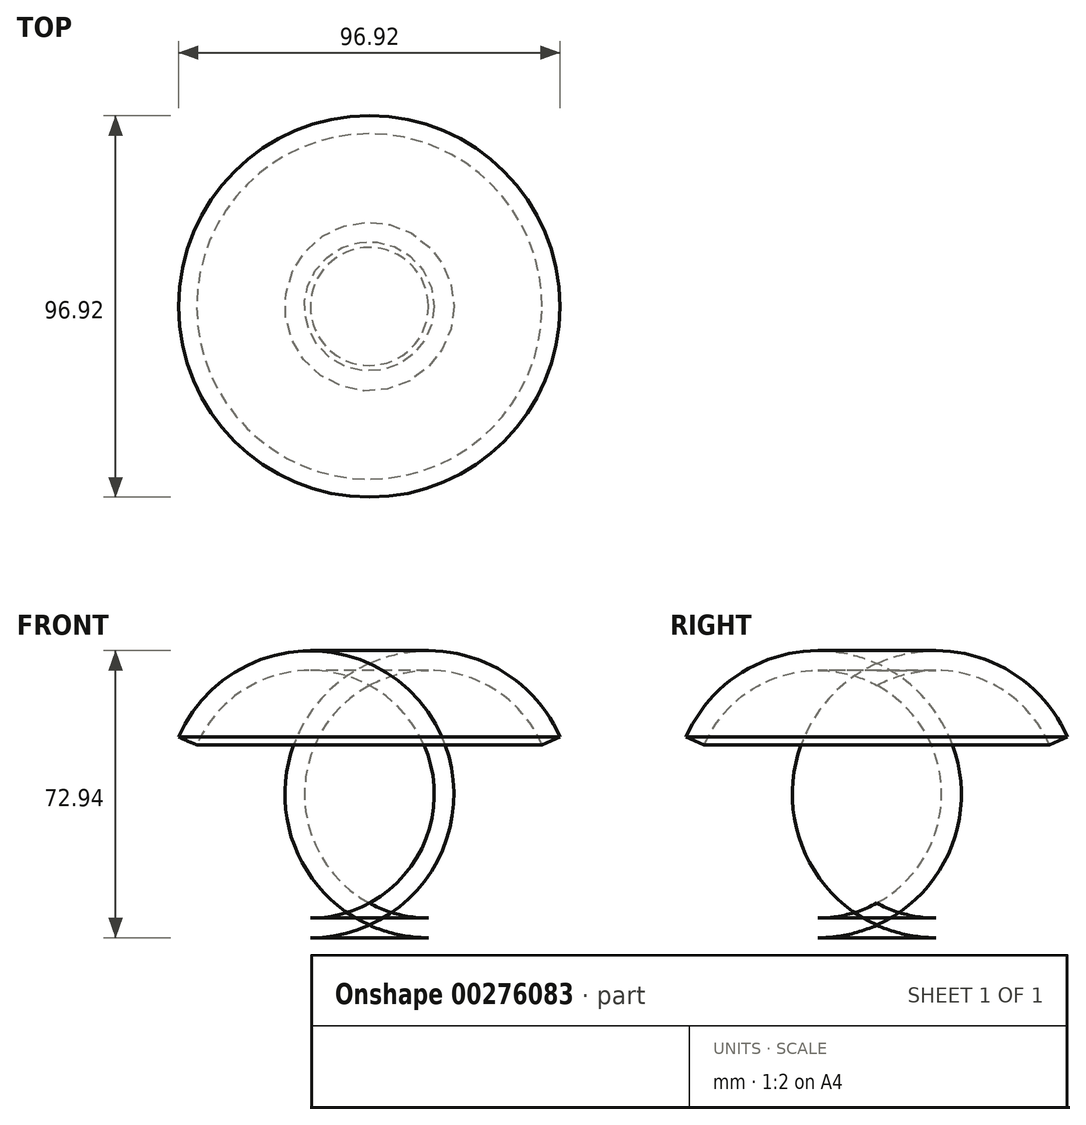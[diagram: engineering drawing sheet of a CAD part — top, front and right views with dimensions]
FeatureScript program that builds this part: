
annotation { "Feature Type Name" : "Feature", "Feature Type Description" : "" }
export const myFeature = defineFeature(function(context is Context, id is Id, definition is map)
    precondition{}
    {
        {
            var Q0;
            Q0=qCreatedBy(makeId("Front.planeOp"),FACE);
            var sketch = newSketch(context, id + "F0", { "sketchPlane" : qUnion([Q0])});
            skLineSegment(sketch, "E0", {"start": v(0, 0) * mm, "end": v(15, 0) * mm});
            skArc(sketch, "E1", {"start": v(15, 0) * mm, "mid": v(41.31, 14.2) * mm, "end": v(43.87, 44) * mm});
            skArc(sketch, "E2.0", {"start": v(15, -5) * mm, "mid": v(45.5, 11.46) * mm, "end": v(48.46, 45.99) * mm});
            skLineSegment(sketch, "E2.1", {"start": v(0, -5) * mm, "end": v(15, -5) * mm});
            skLineSegment(sketch, "E3", {"start": v(43.87, 44) * mm, "end": v(48.46, 45.99) * mm});
            skLineSegment(sketch, "E4", {"start": v(0, -5) * mm, "end": v(0, 0) * mm});
            skSolve(sketch);
        }
        {
            var Q0;
            Q0=makeQuery(id+"F0.imprint","IMPRINT",FACE,{"disambiguationData":[TD([[makeQuery(id+"F0.imprint","IMPRINT",EDGE,{"derivedFrom":sQuery(id+"F0.wireOp",EDGE,"E0")}),-1.0]])]});
            var Q1;
            Q1=sQuery(id+"F0.wireOp",EDGE,"E4");
            revolve(context, id + "F1", {"entities" : qUnion([Q0]), "axis" : qUnion([Q1]), "revolveType" : RevolveType.FULL});
        }
    });
